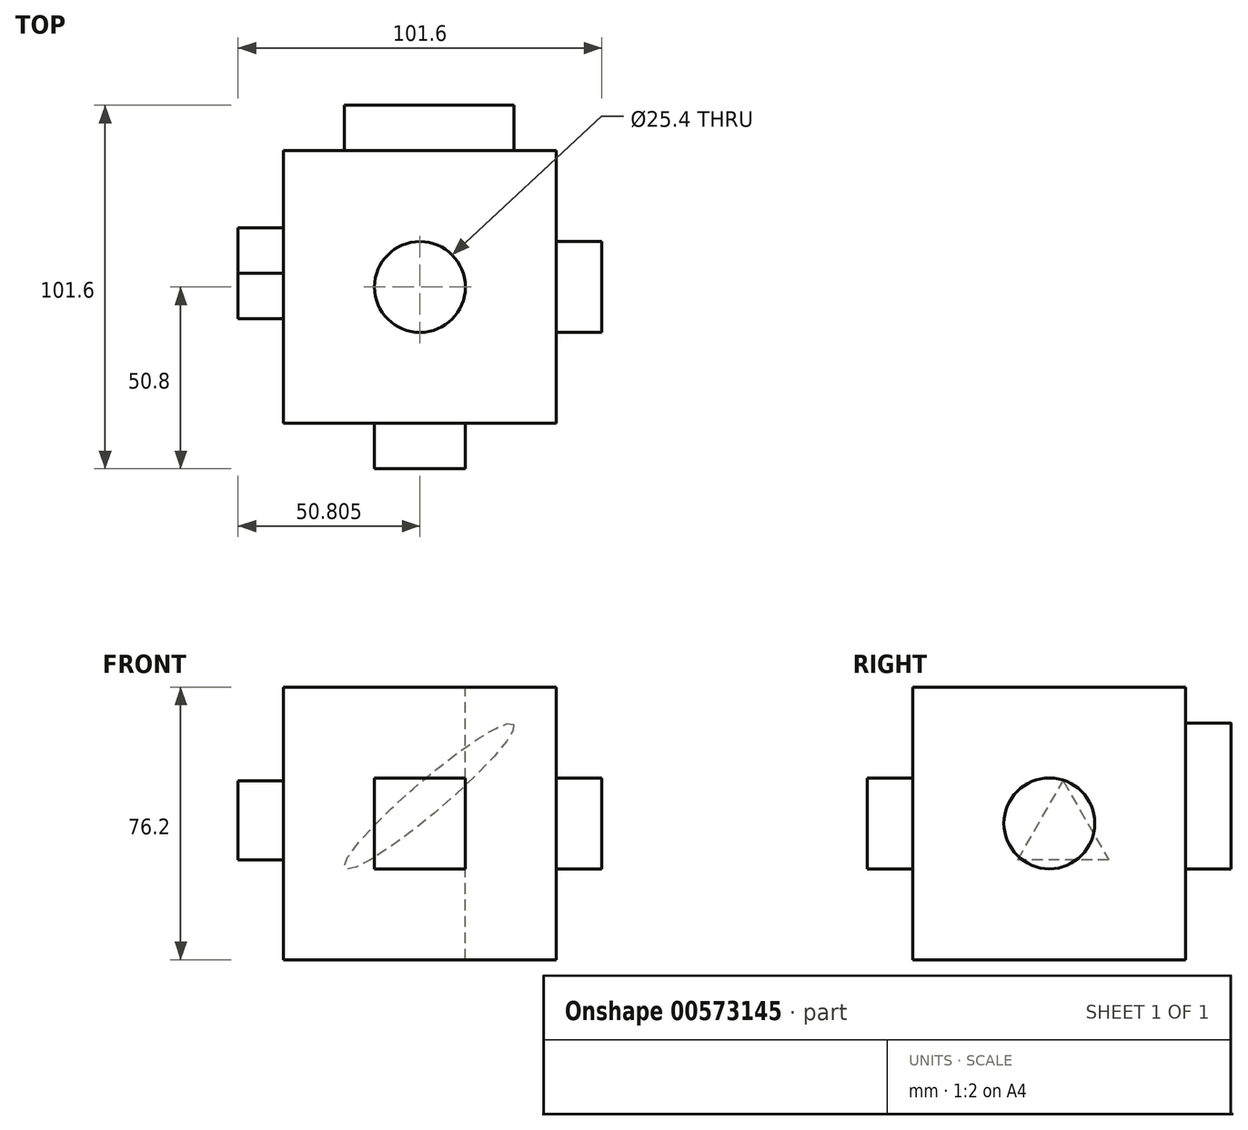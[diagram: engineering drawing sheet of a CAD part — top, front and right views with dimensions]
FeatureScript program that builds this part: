
annotation { "Feature Type Name" : "Feature", "Feature Type Description" : "" }
export const myFeature = defineFeature(function(context is Context, id is Id, definition is map)
    precondition{}
    {
        {
            var Q0;
            Q0=qCreatedBy(makeId("Front.planeOp"),FACE);
            var sketch = newSketch(context, id + "F0", { "sketchPlane" : qUnion([Q0])});
            skLineSegment(sketch, "E0.bottom", {"start": v(-63.2, 66.16) * mm, "end": v(13, 66.16) * mm});
            skLineSegment(sketch, "E0.top", {"start": v(-63.2, -10.04) * mm, "end": v(13, -10.04) * mm});
            skLineSegment(sketch, "E0.left", {"start": v(-63.2, 66.16) * mm, "end": v(-63.2, -10.04) * mm});
            skLineSegment(sketch, "E0.right", {"start": v(13, 66.16) * mm, "end": v(13, -10.04) * mm});
            skSolve(sketch);
        }
        {
            var Q0;
            Q0=makeQuery(id+"F0.imprint","IMPRINT",FACE,{"disambiguationData":[TD([[makeQuery(id+"F0.imprint","IMPRINT",EDGE,{"derivedFrom":sQuery(id+"F0.wireOp",EDGE,"E0.bottom")}),-1.0]])]});
            extrude(context, id + "F1", {"entities" : qUnion([Q0]), "depth" : 76.2 * mm, "offsetDistance" : 25.4 * mm});
        }
        {
            var Q0;
            Q0=makeQuery(id+"F1.opExtrude","CAP_FACE",FACE,{"disambiguationData":[OSD([sQuery(id+"F0.wireOp",EDGE,"E0.bottom"),sQuery(id+"F0.wireOp",EDGE,"E0.top"),sQuery(id+"F0.wireOp",EDGE,"E0.left"),sQuery(id+"F0.wireOp",EDGE,"E0.right")])],"isStart":false});
            var sketch = newSketch(context, id + "F2", { "sketchPlane" : qUnion([Q0])});
            skLineSegment(sketch, "E1.bottom", {"start": v(-37.8, 40.76) * mm, "end": v(-12.4, 40.76) * mm});
            skLineSegment(sketch, "E1.top", {"start": v(-37.8, 15.36) * mm, "end": v(-12.4, 15.36) * mm});
            skLineSegment(sketch, "E1.left", {"start": v(-37.8, 40.76) * mm, "end": v(-37.8, 15.36) * mm});
            skLineSegment(sketch, "E1.right", {"start": v(-12.4, 40.76) * mm, "end": v(-12.4, 15.36) * mm});
            skSolve(sketch);
        }
        {
            var Q0;
            Q0=makeQuery(id+"F2.imprint","IMPRINT",FACE,{"disambiguationData":[TD([[makeQuery(id+"F2.imprint","IMPRINT",EDGE,{"derivedFrom":sQuery(id+"F2.wireOp",EDGE,"E1.bottom")}),-1.0]])]});
            extrude(context, id + "F3", {"entities" : qUnion([Q0]), "operationType" : NewBodyOperationType.ADD, "depth" : 12.7 * mm, "offsetDistance" : 25.4 * mm});
        }
        {
            var Q0;
            Q0=makeQuery(id+"F1.opExtrude","SWEPT_FACE",FACE,{"disambiguationData":[OSD([sQuery(id+"F0.wireOp",EDGE,"E0.right")])]});
            var sketch = newSketch(context, id + "F4", { "sketchPlane" : qUnion([Q0])});
            skCircle(sketch, "E2", {"center": v(-38.1, 28.06) * mm, "radius": 12.7 * mm});
            skPoint(sketch, "E2.centerSnap0", {"position": v(0, 28.06) * mm});
            skSolve(sketch);
        }
        {
            var Q0;
            Q0=makeQuery(id+"F4.imprint","IMPRINT",FACE,{"disambiguationData":[TD([[makeQuery(id+"F4.imprint","IMPRINT",EDGE,{"derivedFrom":sQuery(id+"F4.wireOp",EDGE,"E2")}),1.0]])]});
            extrude(context, id + "F5", {"entities" : qUnion([Q0]), "operationType" : NewBodyOperationType.ADD, "depth" : 12.7 * mm, "offsetDistance" : 25.4 * mm});
        }
        {
            var Q0;
            Q0=makeQuery(id+"F1.opExtrude","SWEPT_FACE",FACE,{"disambiguationData":[OSD([sQuery(id+"F0.wireOp",EDGE,"E0.bottom")])]});
            var sketch = newSketch(context, id + "F6", { "sketchPlane" : qUnion([Q0])});
            skPoint(sketch, "E3", {"position": v(-25.1, -38.1) * mm});
            skSolve(sketch);
        }
        {
            var Q0;
            Q0=sQuery(id+"F6.wireOp",VERTEX,"E3");
            var Q1;
            Q1=makeQuery(id+"F1.opExtrude","SWEPT_BODY",BODY,{"disambiguationData":[OSD([sQuery(id+"F0.wireOp",EDGE,"E0.bottom"),sQuery(id+"F0.wireOp",EDGE,"E0.top"),sQuery(id+"F0.wireOp",EDGE,"E0.left"),sQuery(id+"F0.wireOp",EDGE,"E0.right")])]});
            hole(context, id + "F7", {"style" : HoleStyle.SIMPLE, "endStyle" : HoleEndStyle.THROUGH, "holeDiameter" : 25.4 * mm, "isTappedThrough" : true, "tappedDepth" : 12.7 * mm, "tapClearance" : 3, "locations" : qUnion([Q0]), "scope" : qUnion([Q1])});
        }
        {
            var Q0;
            Q0=makeQuery(id+"F1.opExtrude","SWEPT_FACE",FACE,{"disambiguationData":[OSD([sQuery(id+"F0.wireOp",EDGE,"E0.left")])]});
            var sketch = newSketch(context, id + "F8", { "sketchPlane" : qUnion([Q0])});
            skLineSegment(sketch, "E4", {"start": v(34.26, 39.9) * mm, "end": v(21.56, 17.9) * mm});
            skLineSegment(sketch, "E5", {"start": v(21.56, 17.9) * mm, "end": v(46.96, 17.9) * mm});
            skLineSegment(sketch, "E6", {"start": v(46.96, 17.9) * mm, "end": v(34.26, 39.9) * mm});
            skSolve(sketch);
        }
        {
            var Q0;
            Q0=makeQuery(id+"F8.imprint","IMPRINT",FACE,{"disambiguationData":[TD([[makeQuery(id+"F8.imprint","IMPRINT",EDGE,{"derivedFrom":sQuery(id+"F8.wireOp",EDGE,"E4")}),1.0]])]});
            extrude(context, id + "F9", {"entities" : qUnion([Q0]), "operationType" : NewBodyOperationType.ADD, "depth" : 12.7 * mm, "offsetDistance" : 25.4 * mm});
        }
        {
            var Q0;
            Q0=makeQuery(id+"F1.opExtrude","CAP_FACE",FACE,{"disambiguationData":[OSD([sQuery(id+"F0.wireOp",EDGE,"E0.bottom"),sQuery(id+"F0.wireOp",EDGE,"E0.top"),sQuery(id+"F0.wireOp",EDGE,"E0.left"),sQuery(id+"F0.wireOp",EDGE,"E0.right")])],"isStart":true});
            var sketch = newSketch(context, id + "F10", { "sketchPlane" : qUnion([Q0])});
            skEllipse(sketch, "E7", {"center": v(22.54, 35.65) * mm, "majorRadius": 30.93 * mm, "minorRadius": 4.51 * mm, "majorAxis": v(-0.76, 0.65)});
            skSolve(sketch);
        }
        {
            var Q0;
            Q0=makeQuery(id+"F10.imprint","IMPRINT",FACE,{"disambiguationData":[TD([[makeQuery(id+"F10.imprint","IMPRINT",EDGE,{"derivedFrom":sQuery(id+"F10.wireOp",EDGE,"E7")}),1.0]])]});
            extrude(context, id + "F11", {"entities" : qUnion([Q0]), "operationType" : NewBodyOperationType.ADD, "depth" : 12.7 * mm, "offsetDistance" : 25.4 * mm});
        }
    });
